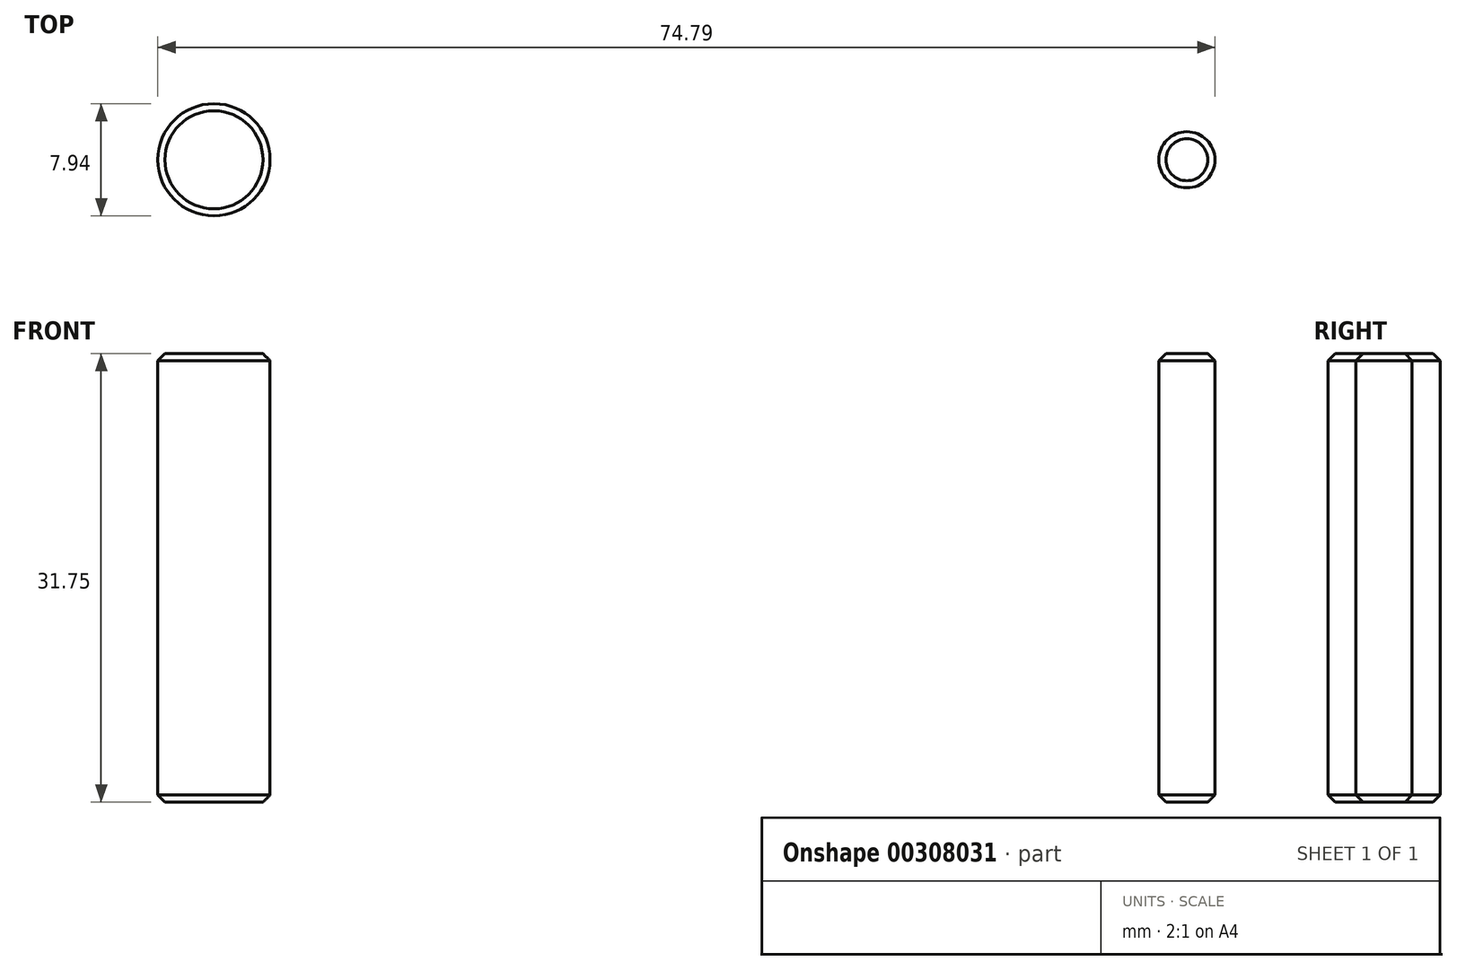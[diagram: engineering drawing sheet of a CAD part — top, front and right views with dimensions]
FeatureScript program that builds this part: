
annotation { "Feature Type Name" : "Feature", "Feature Type Description" : "" }
export const myFeature = defineFeature(function(context is Context, id is Id, definition is map)
    precondition{}
    {
        {
            var Q0;
            Q0=qCreatedBy(makeId("Top.planeOp"),FACE);
            var sketch = newSketch(context, id + "F0", { "sketchPlane" : qUnion([Q0])});
            skCircle(sketch, "E0", {"center": v(-38.55, 0) * mm, "radius": 3.97 * mm});
            skCircle(sketch, "E1", {"center": v(30.28, 0) * mm, "radius": 1.98 * mm});
            skSolve(sketch);
        }
        {
            var Q0;
            Q0=makeQuery(id+"F0.imprint","IMPRINT",FACE,{"disambiguationData":[TD([[makeQuery(id+"F0.imprint","IMPRINT",EDGE,{"derivedFrom":sQuery(id+"F0.wireOp",EDGE,"E0")}),1.0]])]});
            extrude(context, id + "F1", {"entities" : qUnion([Q0]), "depth" : 31.75 * mm});
        }
        {
            var Q0;
            Q0=makeQuery(id+"F0.imprint","IMPRINT",FACE,{"disambiguationData":[TD([[makeQuery(id+"F0.imprint","IMPRINT",EDGE,{"derivedFrom":sQuery(id+"F0.wireOp",EDGE,"E1")}),1.0]])]});
            extrude(context, id + "F2", {"entities" : qUnion([Q0]), "depth" : 31.75 * mm});
        }
        {
            var Q0;
            Q0=makeQuery(id+"F1.opExtrude","CAP_EDGE",EDGE,{"disambiguationData":[OSD([sQuery(id+"F0.wireOp",EDGE,"E0")])],"isStart":false});
            var Q1;
            Q1=makeQuery(id+"F2.opExtrude","CAP_EDGE",EDGE,{"disambiguationData":[OSD([sQuery(id+"F0.wireOp",EDGE,"E1")])],"isStart":false});
            var Q2;
            Q2=makeQuery(id+"F2.opExtrude","CAP_EDGE",EDGE,{"disambiguationData":[OSD([sQuery(id+"F0.wireOp",EDGE,"E1")])],"isStart":true});
            var Q3;
            Q3=makeQuery(id+"F1.opExtrude","CAP_EDGE",EDGE,{"disambiguationData":[OSD([sQuery(id+"F0.wireOp",EDGE,"E0")])],"isStart":true});
            chamfer(context, id + "F3", {"entities" : qUnion([Q0, Q1, Q2, Q3]), "width" : 0.5 * mm, "tangentPropagation" : true});
        }
    });
